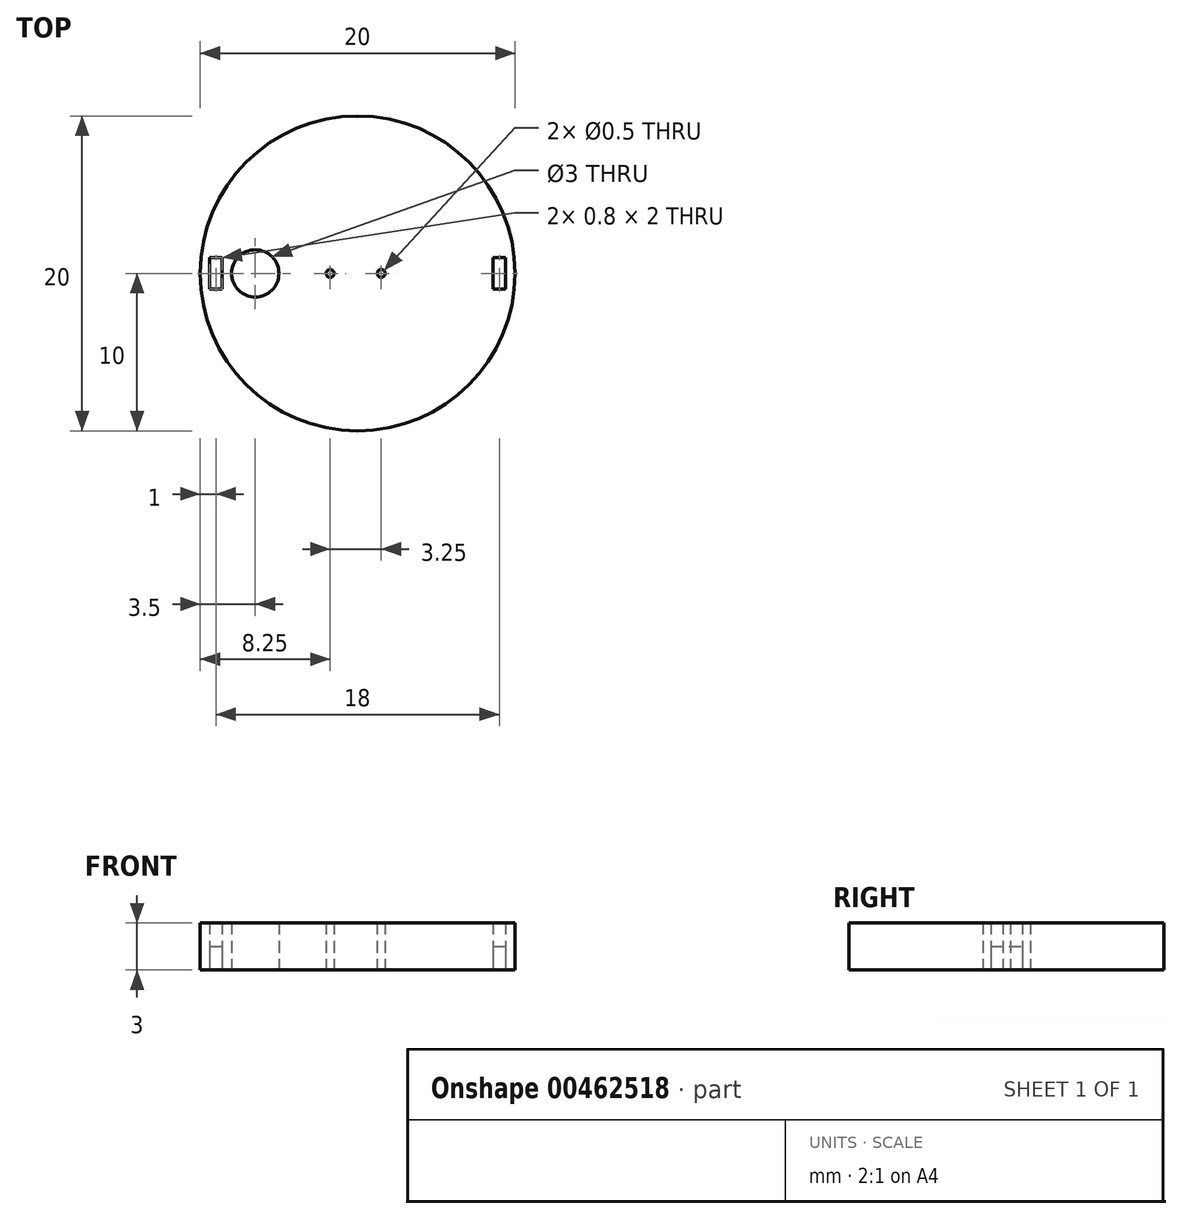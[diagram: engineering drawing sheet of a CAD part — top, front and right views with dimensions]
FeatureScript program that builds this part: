
annotation { "Feature Type Name" : "Feature", "Feature Type Description" : "" }
export const myFeature = defineFeature(function(context is Context, id is Id, definition is map)
    precondition{}
    {
        {
            var Q0;
            Q0=qCreatedBy(makeId("Top.planeOp"),FACE);
            var sketch = newSketch(context, id + "F0", { "sketchPlane" : qUnion([Q0])});
            skCircle(sketch, "E0", {"center": v(0, 0) * mm, "radius": 10 * mm});
            skCircle(sketch, "E1", {"center": v(-1.75, 0) * mm, "radius": 0.25 * mm});
            skCircle(sketch, "E2", {"center": v(1.5, 0) * mm, "radius": 0.25 * mm});
            skCircle(sketch, "E3", {"center": v(-6.5, 0) * mm, "radius": 1.5 * mm});
            skLineSegment(sketch, "E4.bottom", {"start": v(-9.4, -1) * mm, "end": v(-8.6, -1) * mm});
            skLineSegment(sketch, "E4.top", {"start": v(-9.4, 1) * mm, "end": v(-8.6, 1) * mm});
            skLineSegment(sketch, "E4.left", {"start": v(-9.4, -1) * mm, "end": v(-9.4, 1) * mm});
            skLineSegment(sketch, "E4.right", {"start": v(-8.6, -1) * mm, "end": v(-8.6, 1) * mm});
            skLineSegment(sketch, "E5.bottom", {"start": v(8.6, -1) * mm, "end": v(9.4, -1) * mm});
            skLineSegment(sketch, "E5.top", {"start": v(8.6, 1) * mm, "end": v(9.4, 1) * mm});
            skLineSegment(sketch, "E5.left", {"start": v(8.6, -1) * mm, "end": v(8.6, 1) * mm});
            skLineSegment(sketch, "E5.right", {"start": v(9.4, -1) * mm, "end": v(9.4, 1) * mm});
            skSolve(sketch);
        }
        {
            var Q0;
            Q0=makeQuery(id+"F0.imprint","IMPRINT",FACE,{"disambiguationData":[TD([[makeQuery(id+"F0.imprint","IMPRINT",EDGE,{"derivedFrom":sQuery(id+"F0.wireOp",EDGE,"E0")}),1.0]])]});
            extrude(context, id + "F1", {"entities" : qUnion([Q0]), "depth" : 3 * mm});
        }
        {
            var Q0;
            Q0=makeQuery(id+"F0.imprint","IMPRINT",FACE,{"disambiguationData":[TD([[makeQuery(id+"F0.imprint","IMPRINT",EDGE,{"derivedFrom":sQuery(id+"F0.wireOp",EDGE,"E4.bottom")}),1.0]])]});
            var Q1;
            Q1=makeQuery(id+"F0.imprint","IMPRINT",FACE,{"disambiguationData":[TD([[makeQuery(id+"F0.imprint","IMPRINT",EDGE,{"derivedFrom":sQuery(id+"F0.wireOp",EDGE,"E5.bottom")}),1.0]])]});
            extrude(context, id + "F2", {"entities" : qUnion([Q0, Q1]), "depth" : 1.5 * mm});
        }
    });
